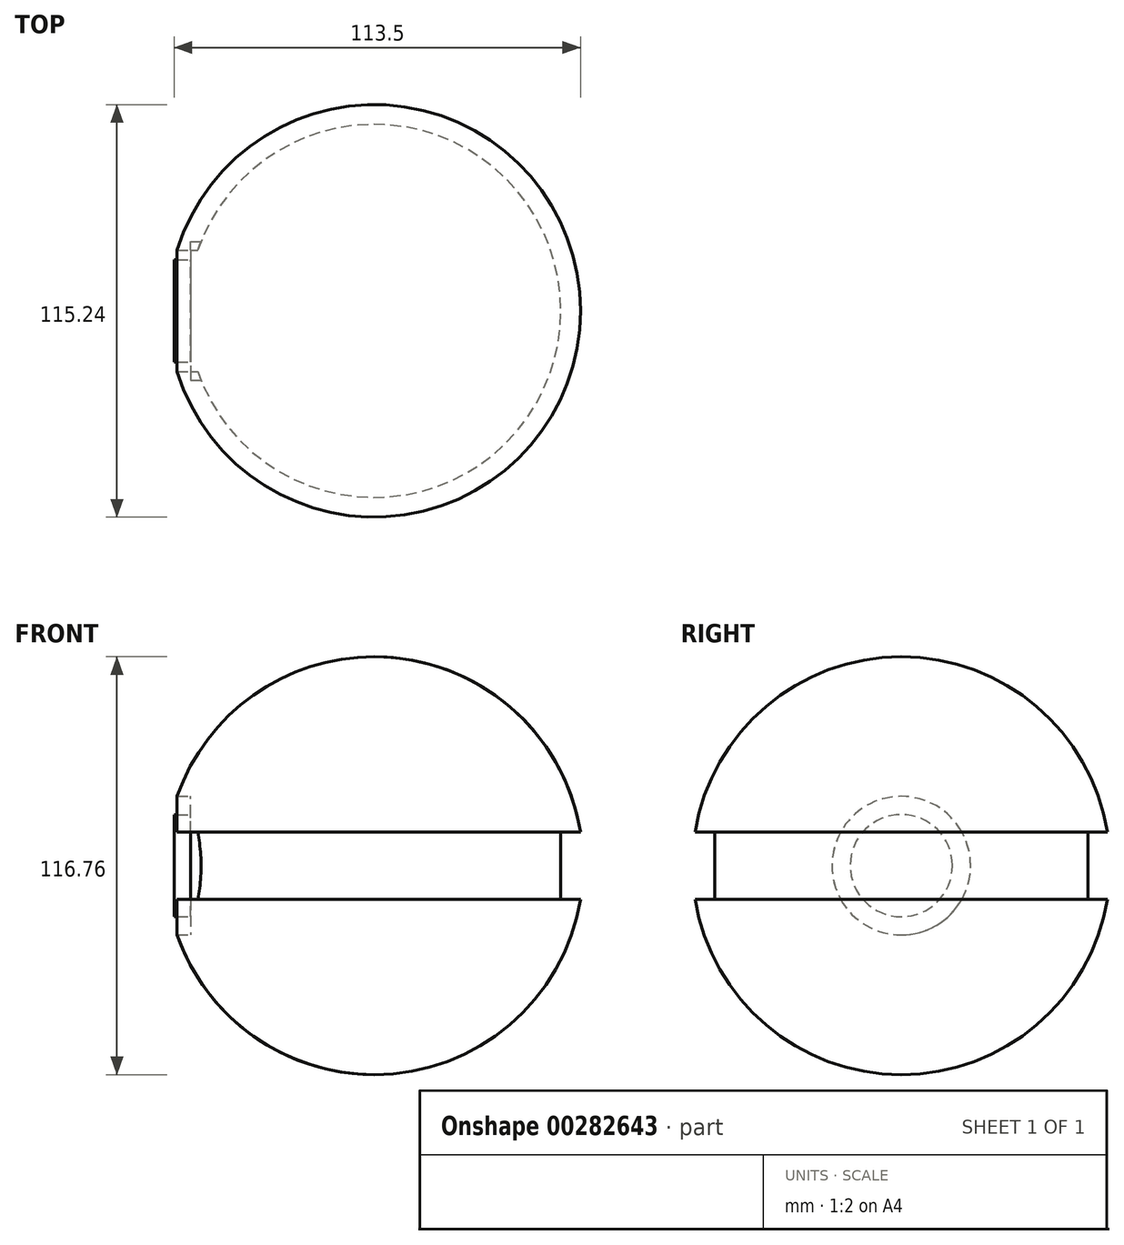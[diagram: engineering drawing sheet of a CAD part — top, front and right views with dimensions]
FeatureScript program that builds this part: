
annotation { "Feature Type Name" : "Feature", "Feature Type Description" : "" }
export const myFeature = defineFeature(function(context is Context, id is Id, definition is map)
    precondition{}
    {
        {
            var Q0;
            Q0=qCreatedBy(makeId("Front.planeOp"),FACE);
            var sketch = newSketch(context, id + "F0", { "sketchPlane" : qUnion([Q0])});
            skCircle(sketch, "E0", {"center": v(0, 0) * mm, "radius": 58.38 * mm});
            skLineSegment(sketch, "E1.bottom", {"start": v(64.65, -9.42) * mm, "end": v(52.12, -9.42) * mm});
            skLineSegment(sketch, "E1.top", {"start": v(64.65, 9.42) * mm, "end": v(52.12, 9.42) * mm});
            skLineSegment(sketch, "E1.left", {"start": v(64.65, -9.42) * mm, "end": v(64.65, 9.42) * mm});
            skLineSegment(sketch, "E1.right", {"start": v(52.12, -9.42) * mm, "end": v(52.12, 9.42) * mm});
            skPoint(sketch, "E1.middle", {"position": v(58.38, 0) * mm});
            skLineSegment(sketch, "E2", {"start": v(0, 58.38) * mm, "end": v(0, -58.38) * mm});
            skSolve(sketch);
        }
        {
            var Q0;
            {var subQ0=sQuery(id+"F0.wireOp",EDGE,"E1.right");Q0=makeQuery(id+"F0.imprint","IMPRINT",FACE,{"disambiguationData":[TD([[makeQuery(id+"F0.imprint","IMPRINT",EDGE,{"derivedFrom":subQ0}),1.0]])]});}
            var Q1;
            Q1=sQuery(id+"F0.wireOp",EDGE,"E2");
            revolve(context, id + "F1", {"entities" : qUnion([Q0]), "axis" : qUnion([Q1]), "revolveType" : RevolveType.FULL});
        }
        {
            var Q0;
            Q0=qCreatedBy(makeId("Right.planeOp"),FACE);
            var sketch = newSketch(context, id + "F2", { "sketchPlane" : qUnion([Q0])});
            skCircle(sketch, "E3", {"center": v(0, 0) * mm, "radius": 19.36 * mm});
            skSolve(sketch);
        }
        {
            var Q0;
            Q0 = qSketchRegion(id + "F2", true);
            extrude(context, id + "F3", {"entities" : qUnion([Q0]), "operationType" : NewBodyOperationType.REMOVE, "endBound" : BoundingType.THROUGH_ALL, "oppositeDirection" : true, "depth" : 25.4 * mm});
        }
        {
            var Q0;
            Q0=qCreatedBy(makeId("Right.planeOp"),FACE);
            var sketch = newSketch(context, id + "F4", { "sketchPlane" : qUnion([Q0])});
            skCircle(sketch, "E4", {"center": v(0, 0) * mm, "radius": 14.27 * mm});
            skSolve(sketch);
        }
        {
            var Q0;
            Q0 = qSketchRegion(id + "F4", true);
            extrude(context, id + "F5", {"entities" : qUnion([Q0]), "operationType" : NewBodyOperationType.ADD, "oppositeDirection" : true, "depth" : 55.88 * mm});
        }
        {
            var Q0;
            Q0 = qSketchRegion(id + "F2", true);
            extrude(context, id + "F6", {"entities" : qUnion([Q0]), "operationType" : NewBodyOperationType.ADD, "oppositeDirection" : true, "depth" : 51.3 * mm});
        }
    });
